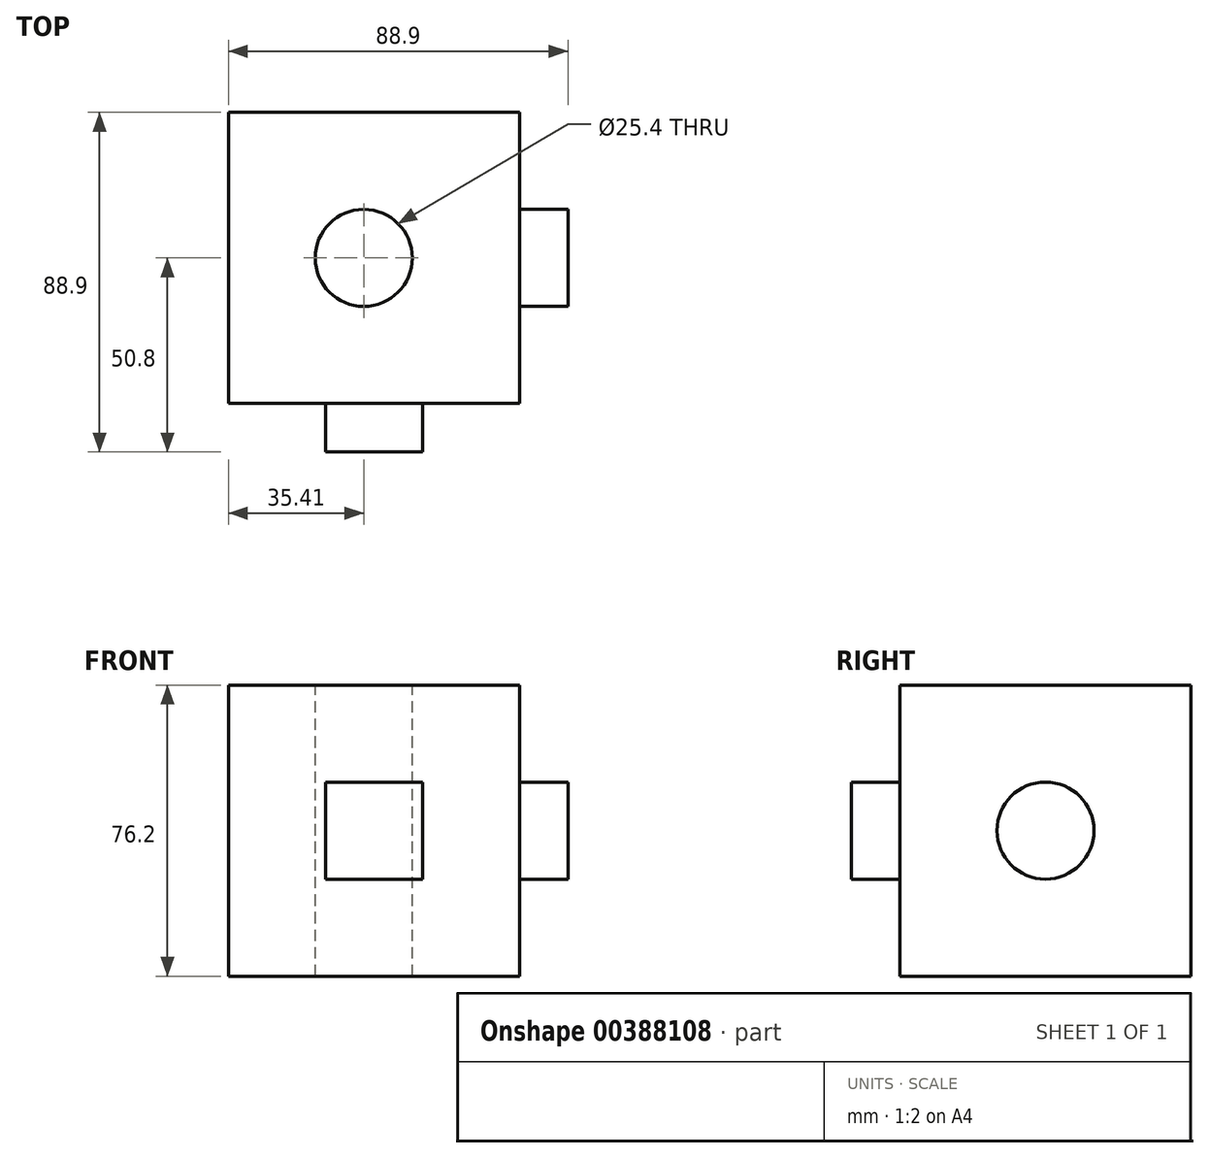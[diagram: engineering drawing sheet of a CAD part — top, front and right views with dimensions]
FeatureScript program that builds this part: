
annotation { "Feature Type Name" : "Feature", "Feature Type Description" : "" }
export const myFeature = defineFeature(function(context is Context, id is Id, definition is map)
    precondition{}
    {
        {
            var Q0;
            Q0=qCreatedBy(makeId("Front.planeOp"),FACE);
            var sketch = newSketch(context, id + "F0", { "sketchPlane" : qUnion([Q0])});
            skLineSegment(sketch, "E0.bottom", {"start": v(-35.41, 32.36) * mm, "end": v(40.79, 32.36) * mm});
            skLineSegment(sketch, "E0.top", {"start": v(-35.41, -43.84) * mm, "end": v(40.79, -43.84) * mm});
            skLineSegment(sketch, "E0.left", {"start": v(-35.41, 32.36) * mm, "end": v(-35.41, -43.84) * mm});
            skLineSegment(sketch, "E0.right", {"start": v(40.79, 32.36) * mm, "end": v(40.79, -43.84) * mm});
            skSolve(sketch);
        }
        {
            var Q0;
            Q0 = qSketchRegion(id + "F0", true);
            extrude(context, id + "F1", {"entities" : qUnion([Q0]), "depth" : 76.2 * mm});
        }
        {
            var Q0;
            Q0=makeQuery(id+"F1.opExtrude","SWEPT_FACE",FACE,{"disambiguationData":[OSD([sQuery(id+"F0.wireOp",EDGE,"E0.bottom")])]});
            var sketch = newSketch(context, id + "F2", { "sketchPlane" : qUnion([Q0])});
            skPoint(sketch, "E1", {"position": v(0, -38.1) * mm});
            skSolve(sketch);
        }
        {
            var Q0;
            Q0=sQuery(id+"F2.wireOp",VERTEX,"E1");
            var Q1;
            Q1=makeQuery(id+"F1.opExtrude","SWEPT_BODY",BODY,{"disambiguationData":[OSD([sQuery(id+"F0.wireOp",EDGE,"E0.bottom"),sQuery(id+"F0.wireOp",EDGE,"E0.top"),sQuery(id+"F0.wireOp",EDGE,"E0.left"),sQuery(id+"F0.wireOp",EDGE,"E0.right")])]});
            hole(context, id + "F3", {"style" : HoleStyle.SIMPLE, "endStyle" : HoleEndStyle.THROUGH, "holeDiameter" : 25.4 * mm, "isTappedThrough" : true, "tappedDepth" : 12.7 * mm, "tapClearance" : 3, "locations" : qUnion([Q0]), "scope" : qUnion([Q1])});
        }
        {
            var Q0;
            Q0=makeQuery(id+"F1.opExtrude","CAP_FACE",FACE,{"disambiguationData":[OSD([sQuery(id+"F0.wireOp",EDGE,"E0.bottom"),sQuery(id+"F0.wireOp",EDGE,"E0.top"),sQuery(id+"F0.wireOp",EDGE,"E0.left"),sQuery(id+"F0.wireOp",EDGE,"E0.right")])],"isStart":false});
            var sketch = newSketch(context, id + "F4", { "sketchPlane" : qUnion([Q0])});
            skLineSegment(sketch, "E2.bottom", {"start": v(-10.01, 6.96) * mm, "end": v(15.39, 6.96) * mm});
            skLineSegment(sketch, "E2.top", {"start": v(-10.01, -18.44) * mm, "end": v(15.39, -18.44) * mm});
            skLineSegment(sketch, "E2.left", {"start": v(-10.01, 6.96) * mm, "end": v(-10.01, -18.44) * mm});
            skLineSegment(sketch, "E2.right", {"start": v(15.39, 6.96) * mm, "end": v(15.39, -18.44) * mm});
            skSolve(sketch);
        }
        {
            var Q0;
            Q0 = qSketchRegion(id + "F4", true);
            extrude(context, id + "F5", {"entities" : qUnion([Q0]), "operationType" : NewBodyOperationType.ADD, "depth" : 12.7 * mm});
        }
        {
            var Q0;
            Q0=makeQuery(id+"F1.opExtrude","SWEPT_FACE",FACE,{"disambiguationData":[OSD([sQuery(id+"F0.wireOp",EDGE,"E0.right")])]});
            var sketch = newSketch(context, id + "F6", { "sketchPlane" : qUnion([Q0])});
            skCircle(sketch, "E3", {"center": v(-38.1, -5.74) * mm, "radius": 12.7 * mm});
            skPoint(sketch, "E3.first.point", {"position": v(-47.16, 3.16) * mm});
            skPoint(sketch, "E3.second.point", {"position": v(-28.16, -13.65) * mm});
            skPoint(sketch, "E3.third.point", {"position": v(-42.64, 6.12) * mm});
            skSolve(sketch);
        }
        {
            var Q0;
            Q0 = qSketchRegion(id + "F6", true);
            extrude(context, id + "F7", {"entities" : qUnion([Q0]), "operationType" : NewBodyOperationType.ADD, "depth" : 12.7 * mm});
        }
    });
